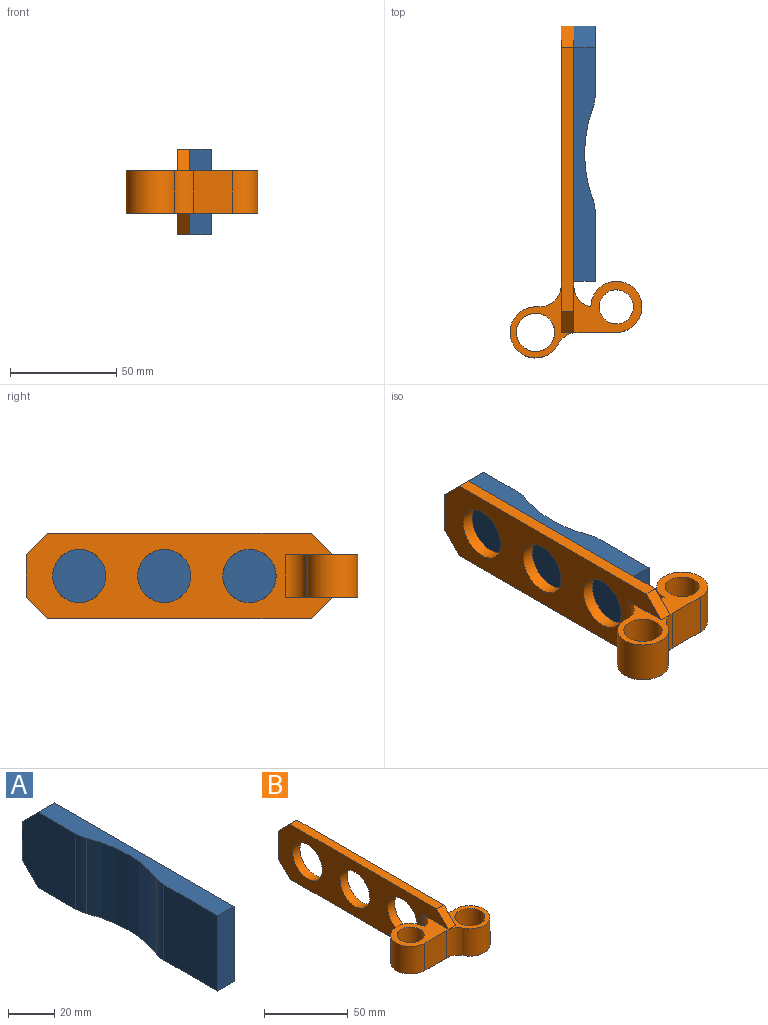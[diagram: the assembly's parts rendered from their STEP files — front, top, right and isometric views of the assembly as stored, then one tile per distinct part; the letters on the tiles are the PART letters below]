
ASSEMBLY  parts=2 mates=1
PART A: 14 faces, bbox 10x120x40 mm
  f0: plane 120x40mm, normal (1,0,0), area 4700mm2, adj f1,f7,f8,f9,f10,f11
  f1: plane 20x10mm, normal (0,1,0), area 200mm2, adj f0,f2,f10,f11
  f2: plane 40x33.07mm, normal (-1,0,0), area 1223mm2, adj f1,f8,f9,f10,f11,f12
  f3: plane 40x0.03mm, normal (-0.93,-0.36,0), area 1.4mm2, adj f4,f8,f9,f12
  f4: cylinder r=60mm len=43.03mm, axis (0,0,1), area 1760.4mm2, adj f3,f5,f8,f9
  f5: plane 40x0.03mm, normal (-0.93,0.36,0), area 1.4mm2, adj f4,f8,f9,f13
  f6: plane 40x33.07mm, normal (-1,0,0), area 1323mm2, adj f7,f8,f9,f13
  f7: plane 40x10mm, normal (0,-1,0), area 400mm2, adj f0,f6,f8,f9
  f8: plane 110x10mm, normal (0,0,-1), area 937.7mm2, adj f0,f2,f3,f4,f5,f6,f7,f10
  f9: plane 110x10mm, normal (0,0,1), area 937.7mm2, adj f0,f2,f3,f4,f5,f6,f7,f11
  f10: plane 10x10mm, normal (0,0.71,-0.71), area 141.4mm2, adj f0,f1,f2,f8
  f11: plane 10x10mm, normal (0,0.71,0.71), area 141.4mm2, adj f0,f1,f2,f9
  f12: cylinder r=15mm len=40mm, axis (0,0,1), area 220mm2, adj f2,f3,f8,f9
  f13: cylinder r=15mm len=40mm, axis (0,0,1), area 220mm2, adj f5,f6,f8,f9
PART B: 23 faces, bbox 62x156x40 mm
  f0: plane 62x36mm, normal (0,0,-1), area 657.3mm2, adj f1,f2,f3,f4,f5,f6,f8,f9
  f1: cylinder r=12mm len=24mm, axis (0,0,1), area 1017.7mm2, adj f0,f3,f7,f21
  f2: cylinder r=9mm len=20mm, axis (0,0,1), area 1131mm2, adj f0,f7
  f3: plane 20x2mm, normal (0,1,0), area 40mm2, adj f0,f1,f7,f22
  f4: plane 20x18.4mm, normal (0,-1,0), area 368.1mm2, adj f0,f5,f7,f21
  f5: cylinder r=12mm len=24mm, axis (0,0,1), area 1131mm2, adj f0,f4,f7,f20
  f6: cylinder r=8mm len=20mm, axis (0,0,1), area 1005.3mm2, adj f0,f7
  f7: plane 62x36mm, normal (0,0,1), area 657.3mm2, adj f1,f2,f3,f4,f5,f6,f8,f9
  f8: plane 144x40mm, normal (1,0,0), area 3647.4mm2, adj f0,f7,f10,f11,f12,f13,f14,f15
  f9: plane 144x40mm, normal (-1,0,0), area 3651.4mm2, adj f0,f7,f10,f11,f12,f13,f14,f15
  f10: plane 20x6mm, normal (0,1,0), area 120mm2, adj f8,f9,f15,f16
  f11: plane 124x6mm, normal (0,0,-1), area 744mm2, adj f8,f9,f13,f15
  f12: plane 124x6mm, normal (0,0,1), area 744mm2, adj f8,f9,f14,f16
  f13: plane 10x10mm, normal (0,-0.71,-0.71), area 84.9mm2, adj f0,f8,f9,f11
  f14: plane 10x10mm, normal (0,-0.71,0.71), area 84.9mm2, adj f7,f8,f9,f12
  f15: plane 10x10mm, normal (0,0.71,-0.71), area 84.9mm2, adj f8,f9,f10,f11
  f16: plane 10x10mm, normal (0,0.71,0.71), area 84.9mm2, adj f8,f9,f10,f12
  f17: cylinder r=12.5mm len=25mm, axis (1,0,0), area 471.2mm2, adj f8,f9
  f18: cylinder r=12.5mm len=25mm, axis (1,0,0), area 471.2mm2, adj f8,f9
  f19: cylinder r=12.5mm len=25mm, axis (1,0,0), area 471.2mm2, adj f8,f9
  f20: cylinder r=10mm len=20mm, axis (0,0,1), area 273.9mm2, adj f0,f5,f7,f9
  f21: cylinder r=10mm len=20mm, axis (0,0,1), area 219.8mm2, adj f0,f1,f4,f7
  f22: cylinder r=10mm len=20mm, axis (0,0,-1), area 314.2mm2, adj f0,f3,f7,f8
PLACE A rot(axis=(0,-1,0),180deg) t=(204.49,-131.88,-30.16)mm
PLACE B rot(axis=(0,-1,0),180deg) t=(204.49,-131.88,-30.16)mm
MATE fastened A.f0 <-> B.f9  axis (-1,0,0) through (59.34,120.96,34.69)mm
